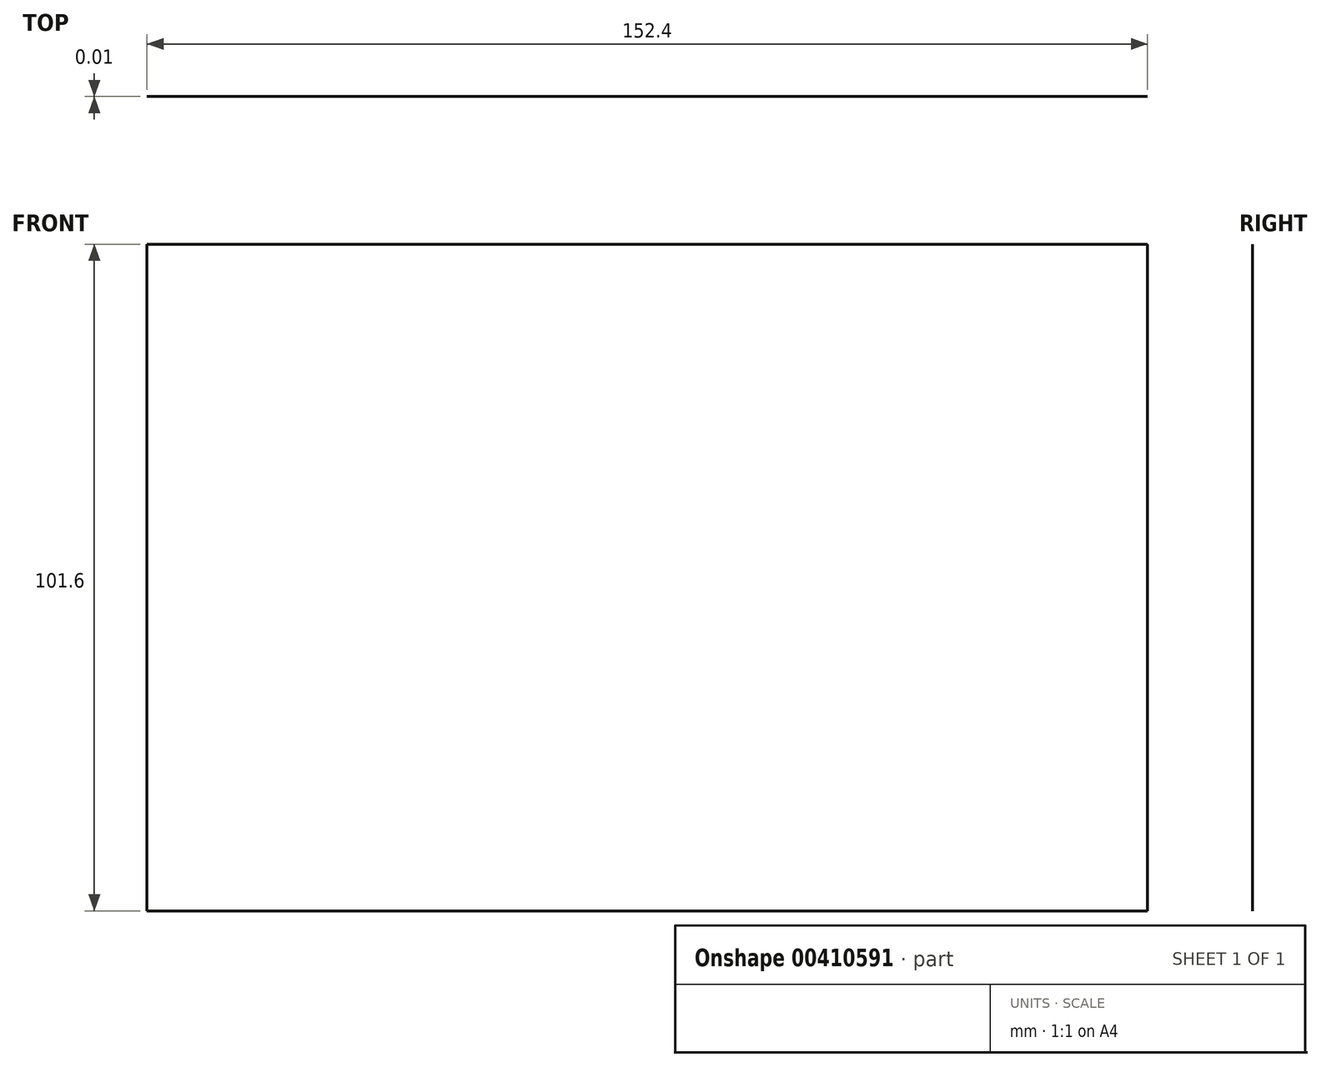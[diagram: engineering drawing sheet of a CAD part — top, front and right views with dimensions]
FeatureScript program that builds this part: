
annotation { "Feature Type Name" : "Feature", "Feature Type Description" : "" }
export const myFeature = defineFeature(function(context is Context, id is Id, definition is map)
    precondition{}
    {
        {
            var Q0;
            Q0=qCreatedBy(makeId("Front.planeOp"), FACE);
            var sketch = newSketch(context, id + "F0", { "sketchPlane" : qUnion([Q0])});
            skLineSegment(sketch, "E0.bottom", {"start": v(-76.2, 50.8) * mm, "end": v(76.2, 50.8) * mm});
            skLineSegment(sketch, "E0.top", {"start": v(-76.2, -50.8) * mm, "end": v(76.2, -50.8) * mm});
            skLineSegment(sketch, "E0.left", {"start": v(-76.2, 50.8) * mm, "end": v(-76.2, -50.8) * mm});
            skLineSegment(sketch, "E0.right", {"start": v(76.2, 50.8) * mm, "end": v(76.2, -50.8) * mm});
            skLineSegment(sketch, "E1", {"start": v(-76.2, 50.8) * mm, "end": v(76.2, -50.8) * mm, "construction": true});
            skPoint(sketch, "E2", {"position": v(0, 0) * mm});
            skSolve(sketch);
        }
        {
            var Q0;
            Q0 = qSketchRegion(id + "F0", true);
            extrude(context, id + "F1", {"entities" : qUnion([Q0]), "depth" : 0 * mm, "offsetDistance" : 25.4 * mm});
        }
    });
